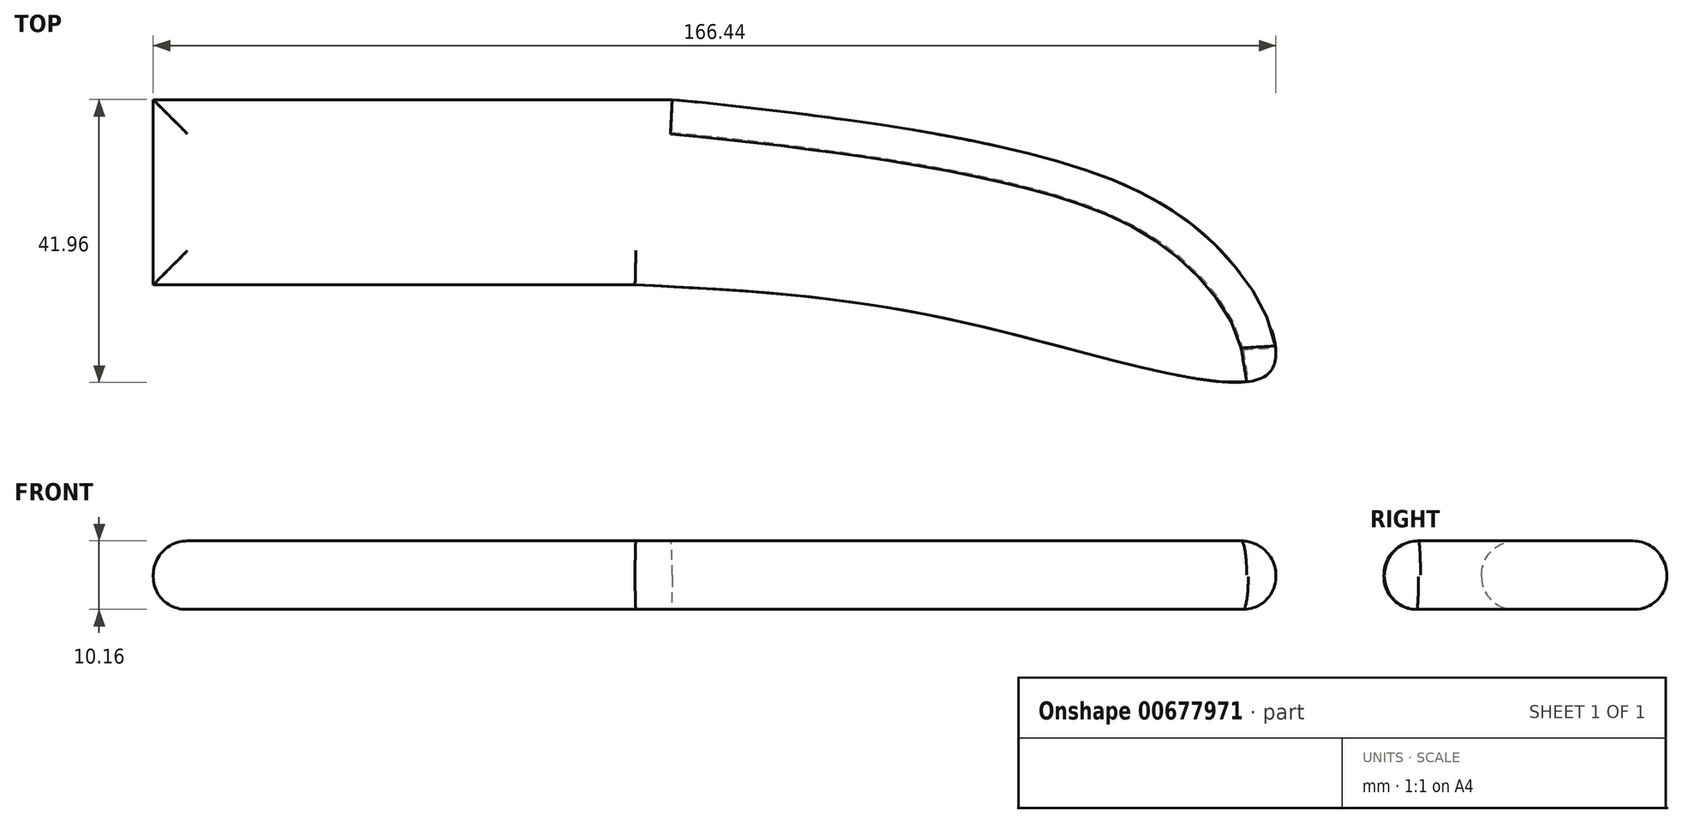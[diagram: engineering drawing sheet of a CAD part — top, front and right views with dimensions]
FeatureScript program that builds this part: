
annotation { "Feature Type Name" : "Feature", "Feature Type Description" : "" }
export const myFeature = defineFeature(function(context is Context, id is Id, definition is map)
    precondition{}
    {
        {
            var Q0;
            Q0=qCreatedBy(makeId("Top.planeOp"),FACE);
            var sketch = newSketch(context, id + "F0", { "sketchPlane" : qUnion([Q0])});
            skLineSegment(sketch, "E0", {"start": v(-94.41, 41.3) * mm, "end": v(-17.48, 41.3) * mm});
            skLineSegment(sketch, "E1", {"start": v(-94.41, 41.3) * mm, "end": v(-94.41, 13.83) * mm});
            skLineSegment(sketch, "E2", {"start": v(-94.41, 13.83) * mm, "end": v(-22.97, 13.83) * mm});
            skFitSpline(sketch, "E3", {"points": [v(-17.48, 41.3) * mm, v(36.38, 33.06) * mm, v(61.1, 21.52) * mm, v(71.55, 6.69) * mm, v(69.9, 0) * mm, v(25.39, 8.33) * mm, v(-22.97, 13.83) * mm], "startDerivative": vector(242.64, -23.45) * mm, "endDerivative": vector(-209.01, 10.08) * mm});
            skPoint(sketch, "E4", {"position": v(-67.49, 13.83) * mm});
            skSolve(sketch);
        }
        {
            var Q0;
            Q0=makeQuery(id+"F0.imprint","IMPRINT",FACE,{"disambiguationData":[TD([[makeQuery(id+"F0.imprint","IMPRINT",EDGE,{"derivedFrom":sQuery(id+"F0.wireOp",EDGE,"E0")}),-1.0]])]});
            extrude(context, id + "F1", {"entities" : qUnion([Q0]), "depth" : 10.16 * mm, "offsetDistance" : 25.4 * mm});
        }
        {
            var Q0;
            Q0=makeQuery(id+"F1.opExtrude","CAP_FACE",FACE,{"disambiguationData":[OSD([sQuery(id+"F0.wireOp",EDGE,"E0"),sQuery(id+"F0.wireOp",EDGE,"E1"),sQuery(id+"F0.wireOp",EDGE,"E2"),sQuery(id+"F0.wireOp",EDGE,"E3")])],"isStart":false});
            fillet(context, id + "F2", {"entities" : qUnion([Q0]), "radius" : 5.08 * mm, "tangentPropagation" : true, "allowEdgeOverflow" : false});
        }
        {
            var Q0;
            Q0=makeQuery(id+"F1.opExtrude","CAP_FACE",FACE,{"disambiguationData":[OSD([sQuery(id+"F0.wireOp",EDGE,"E0"),sQuery(id+"F0.wireOp",EDGE,"E1"),sQuery(id+"F0.wireOp",EDGE,"E2"),sQuery(id+"F0.wireOp",EDGE,"E3")])],"isStart":true});
            fillet(context, id + "F3", {"entities" : qUnion([Q0]), "radius" : 4.83 * mm, "tangentPropagation" : true, "allowEdgeOverflow" : false});
        }
        {
            var Q0;
            Q0=makeQuery(id+"F1.opExtrude","SWEPT_BODY",BODY,{"disambiguationData":[OSD([sQuery(id+"F0.wireOp",EDGE,"E0"),sQuery(id+"F0.wireOp",EDGE,"E1"),sQuery(id+"F0.wireOp",EDGE,"E2"),sQuery(id+"F0.wireOp",EDGE,"E3")])]});
            transform(context, id + "F4", {"entities" : qUnion([Q0]), "transformType" : TransformType.TRANSLATION_3D, "dx" : 0 * mm, "dy" : 27.94 * mm, "dz" : 0 * mm, "makeCopy" : true});
        }
        {
            var Q0;
            Q0=makeQuery(id+"F4.opPattern","COPY",BODY,{"derivedFrom":makeQuery(id+"F1.opExtrude","SWEPT_BODY",BODY,{"disambiguationData":[OSD([sQuery(id+"F0.wireOp",EDGE,"E0"),sQuery(id+"F0.wireOp",EDGE,"E1"),sQuery(id+"F0.wireOp",EDGE,"E2"),sQuery(id+"F0.wireOp",EDGE,"E3")])]}),"instanceName":"1"});
            deleteBodies(context, id + "F5", {"entities" : qUnion([Q0])});
        }
    });
